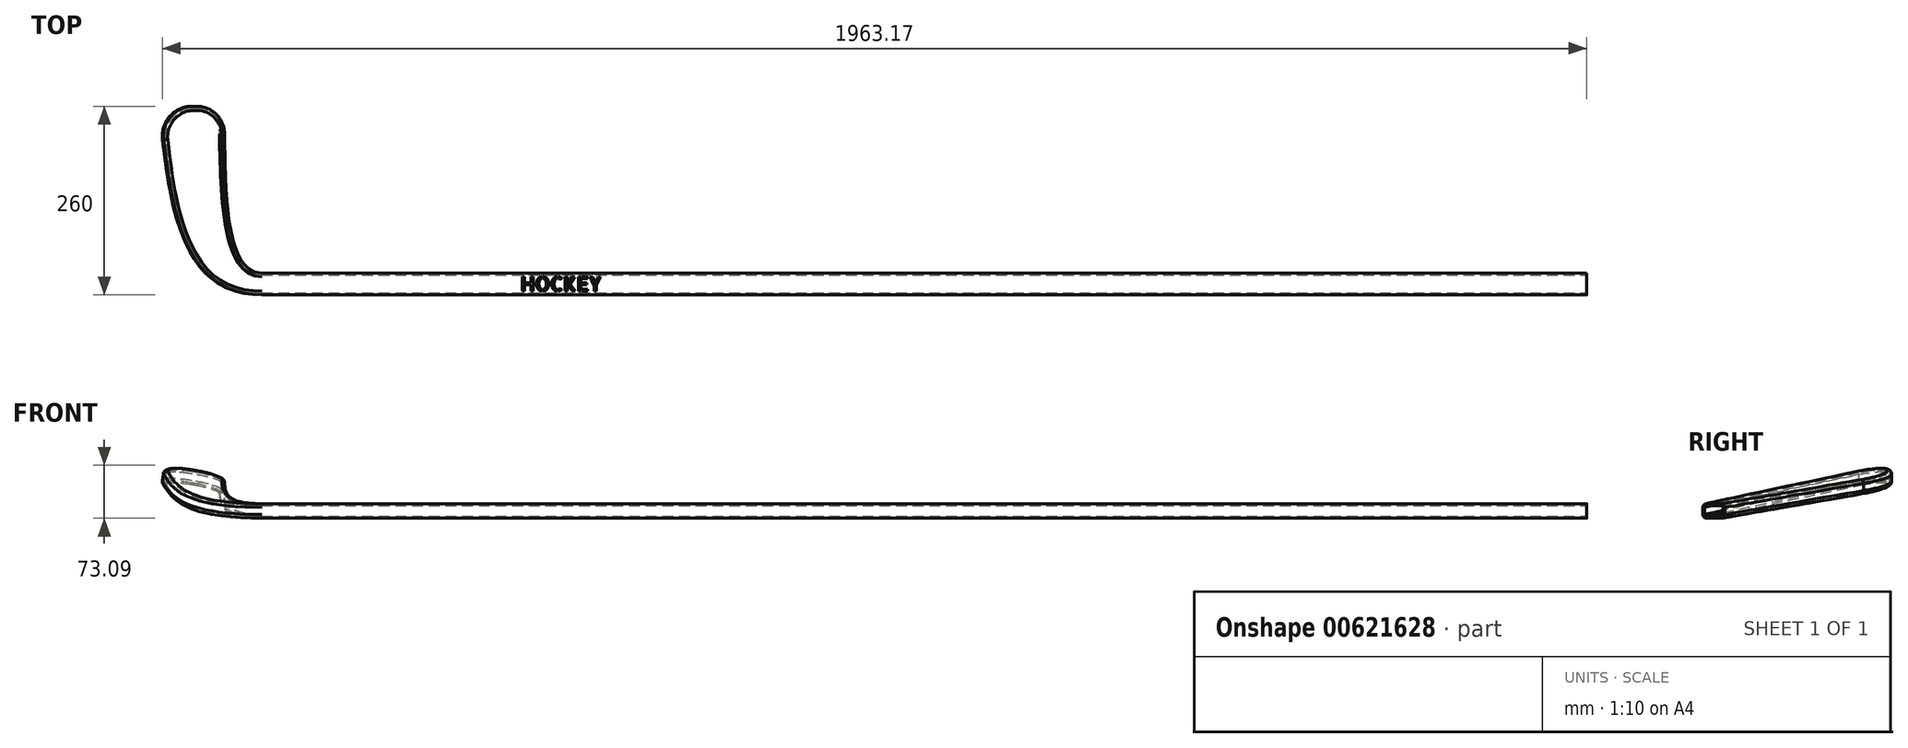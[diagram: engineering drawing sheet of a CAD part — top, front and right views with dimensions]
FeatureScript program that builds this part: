
annotation { "Feature Type Name" : "Feature", "Feature Type Description" : "" }
export const myFeature = defineFeature(function(context is Context, id is Id, definition is map)
    precondition{}
    {
        {
            var Q0;
            Q0=qCreatedBy(makeId("Right.planeOp"),FACE);
            var sketch = newSketch(context, id + "F0", { "sketchPlane" : qUnion([Q0])});
            skLineSegment(sketch, "E0.bottom", {"start": v(0, 0) * mm, "end": v(30, 0) * mm});
            skLineSegment(sketch, "E0.top", {"start": v(0, 20) * mm, "end": v(30, 20) * mm});
            skLineSegment(sketch, "E0.left", {"start": v(0, 0) * mm, "end": v(0, 20) * mm});
            skLineSegment(sketch, "E0.right", {"start": v(30, 0) * mm, "end": v(30, 20) * mm});
            skSolve(sketch);
        }
        {
            var Q0;
            Q0 = qSketchRegion(id + "F0", true);
            extrude(context, id + "F1", {"entities" : qUnion([Q0]), "depth" : 1826 * mm, "offsetDistance" : 25 * mm});
        }
        {
            var Q0;
            Q0=makeQuery(id+"F1.opExtrude","SWEPT_FACE",FACE,{"disambiguationData":[OSD([sQuery(id+"F0.wireOp",EDGE,"E0.right")])]});
            cPlane(context, id + "F2", {"entities" : qUnion([Q0]), "cplaneType" : CPlaneType.OFFSET, "offset" : 230 * mm, "width" : 150 * mm, "height" : 150 * mm});
        }
        {
            var Q0;
            Q0=qCreatedBy(id+"F2.planeOp",FACE);
            var sketch = newSketch(context, id + "F3", { "sketchPlane" : qUnion([Q0])});
            skLineSegment(sketch, "E1.bottom", {"start": v(139.04, 75.29) * mm, "end": v(50.4, 59.66) * mm});
            skLineSegment(sketch, "E1.top", {"start": v(142.51, 55.6) * mm, "end": v(53.88, 39.96) * mm});
            skLineSegment(sketch, "E1.left", {"start": v(139.04, 75.29) * mm, "end": v(142.51, 55.6) * mm});
            skLineSegment(sketch, "E1.right", {"start": v(50.4, 59.66) * mm, "end": v(53.88, 39.96) * mm});
            skSolve(sketch);
        }
        {
            var Q1;
            Q1=makeQuery(id+"F3.imprint","IMPRINT",FACE,{"disambiguationData":[TD([[makeQuery(id+"F3.imprint","IMPRINT",EDGE,{"derivedFrom":sQuery(id+"F3.wireOp",EDGE,"E1.bottom")}),1.0]])]});
            var Q2;
            Q2=makeQuery(id+"F1.opExtrude","CAP_FACE",FACE,{"disambiguationData":[OSD([sQuery(id+"F0.wireOp",EDGE,"E0.bottom"),sQuery(id+"F0.wireOp",EDGE,"E0.top"),sQuery(id+"F0.wireOp",EDGE,"E0.left"),sQuery(id+"F0.wireOp",EDGE,"E0.right")])],"isStart":true});
            loft(context, id + "F4", {"operationType" : NewBodyOperationType.ADD, "endCondition" : LoftEndDerivativeType.NORMAL_TO_PROFILE, "endMagnitude" : 2.2, "sheetProfilesArray" : [{ "sheetProfileEntities" : qUnion([Q1]) }, { "sheetProfileEntities" : qUnion([Q2]) }]});
        }
        {
            var Q0;
            Q0=makeQuery(id+"F4.opLoft","MID_CAP_EDGE",EDGE,{"disambiguationData":[OSD([sQuery(id+"F3.wireOp",EDGE,"E1.bottom"),sQuery(id+"F3.wireOp",EDGE,"E1.top"),sQuery(id+"F3.wireOp",EDGE,"E1.right")])],"capPos":0.0});
            var Q1;
            Q1=makeQuery(id+"F4.opLoft","MID_CAP_EDGE",EDGE,{"disambiguationData":[OSD([sQuery(id+"F3.wireOp",EDGE,"E1.bottom"),sQuery(id+"F3.wireOp",EDGE,"E1.top"),sQuery(id+"F3.wireOp",EDGE,"E1.left")])],"capPos":0.0});
            fillet(context, id + "F5", {"entities" : qUnion([Q0, Q1]), "radius" : 40 * mm, "tangentPropagation" : true, "allowEdgeOverflow" : false});
        }
        {
            var Q0;
            Q0=makeQuery(id+"F4.opLoft","SWEPT_FACE",FACE,{"disambiguationData":[OSD([sQuery(id+"F0.wireOp",EDGE,"E0.top"),sQuery(id+"F0.wireOp",EDGE,"E0.left"),sQuery(id+"F0.wireOp",EDGE,"E0.right"),sQuery(id+"F3.wireOp",EDGE,"E1.bottom"),sQuery(id+"F3.wireOp",EDGE,"E1.left"),sQuery(id+"F3.wireOp",EDGE,"E1.right")])]});
            var Q1;
            Q1=makeQuery(id+"F4.opLoft","SWEPT_FACE",FACE,{"disambiguationData":[OSD([sQuery(id+"F0.wireOp",EDGE,"E0.bottom"),sQuery(id+"F0.wireOp",EDGE,"E0.left"),sQuery(id+"F0.wireOp",EDGE,"E0.right"),sQuery(id+"F3.wireOp",EDGE,"E1.top"),sQuery(id+"F3.wireOp",EDGE,"E1.left"),sQuery(id+"F3.wireOp",EDGE,"E1.right")])]});
            var Q2;
            Q2=makeQuery(id+"F1.opExtrude","SWEPT_EDGE",EDGE,{"disambiguationData":[OSD([sQuery(id+"F0.wireOp",EDGE,"E0.top"),sQuery(id+"F0.wireOp",EDGE,"E0.right")])]});
            var Q3;
            Q3=makeQuery(id+"F1.opExtrude","SWEPT_EDGE",EDGE,{"disambiguationData":[OSD([sQuery(id+"F0.wireOp",EDGE,"E0.bottom"),sQuery(id+"F0.wireOp",EDGE,"E0.right")])]});
            fillet(context, id + "F6", {"entities" : qUnion([Q0, Q1, Q2, Q3]), "radius" : 5 * mm, "tangentPropagation" : true, "allowEdgeOverflow" : false});
        }
        {
            var Q0;
            Q0=makeQuery(id+"F1.opExtrude","SWEPT_FACE",FACE,{"disambiguationData":[OSD([sQuery(id+"F0.wireOp",EDGE,"E0.top")])]});
            var sketch = newSketch(context, id + "F7", { "sketchPlane" : qUnion([Q0])});
            skText(sketch, "E2", { "text": "HOCKEY", "fontName": "AllertaStencil-Regular.ttf"});
            const initialGuessF7  = {"E2": [0.35628, 0.005, 1, 0, 0.02]};
            skSetInitialGuess(sketch, initialGuessF7);
            skSolve(sketch);
        }
        {
            var Q0;
            Q0=makeQuery(id+"F1.opExtrude","CAP_FACE",FACE,{"disambiguationData":[OSD([sQuery(id+"F0.wireOp",EDGE,"E0.bottom"),sQuery(id+"F0.wireOp",EDGE,"E0.top"),sQuery(id+"F0.wireOp",EDGE,"E0.left"),sQuery(id+"F0.wireOp",EDGE,"E0.right")])],"isStart":false});
            shell(context, id + "F8", {"entities" : qUnion([Q0]), "thickness" : 2.5 * mm});
        }
        {
            var Q0;
            Q0 = qSketchRegion(id + "F7", true);
            extrude(context, id + "F9", {"entities" : qUnion([Q0]), "operationType" : NewBodyOperationType.ADD, "depth" : .1 * mm, "offsetDistance" : 25 * mm});
        }
    });
